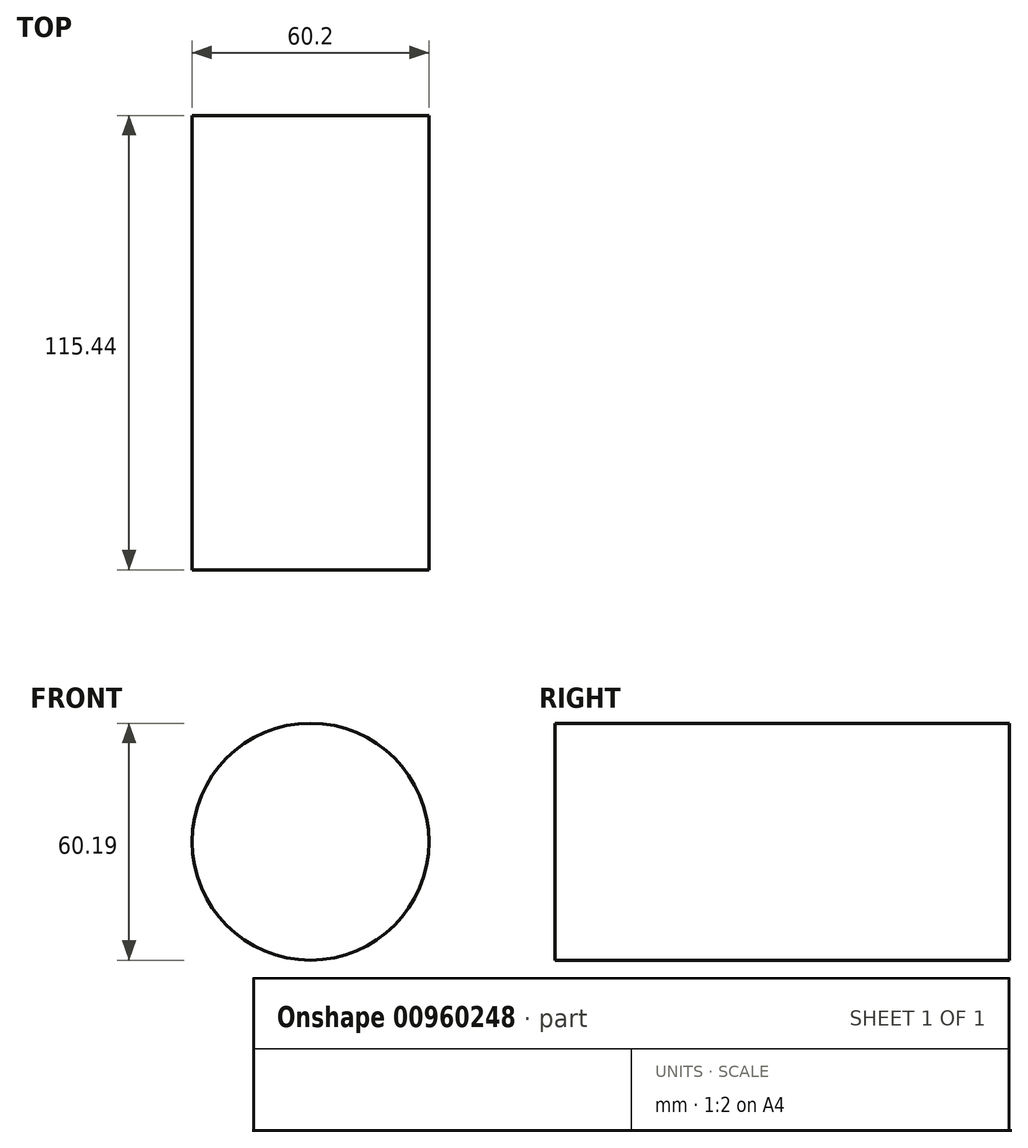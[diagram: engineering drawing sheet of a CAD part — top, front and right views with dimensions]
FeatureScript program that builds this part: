
annotation { "Feature Type Name" : "Feature", "Feature Type Description" : "" }
export const myFeature = defineFeature(function(context is Context, id is Id, definition is map)
    precondition{}
    {
        {
            var Q0;
            Q0=qCreatedBy(makeId("Front.planeOp"),FACE);
            var sketch = newSketch(context, id + "F0", { "sketchPlane" : qUnion([Q0])});
            skCircle(sketch, "E0", {"center": v(59.36, 47.12) * mm, "radius": 30.1 * mm});
            skSolve(sketch);
        }
        {
            var Q0;
            Q0=makeQuery(id+"F0.imprint","IMPRINT",FACE,{"disambiguationData":[TD([[makeQuery(id+"F0.imprint","IMPRINT",EDGE,{"derivedFrom":sQuery(id+"F0.wireOp",EDGE,"E0")}),1.0]])]});
            extrude(context, id + "F1", {"entities" : qUnion([Q0]), "depth" : 115.44 * mm, "offsetDistance" : 25 * mm});
        }
    });
